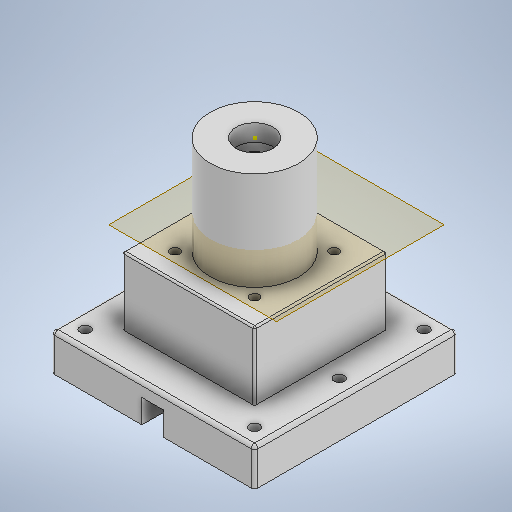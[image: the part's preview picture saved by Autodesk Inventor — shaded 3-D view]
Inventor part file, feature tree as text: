
AUTODESK INVENTOR PART (.ipt)
format: ipt  version: 2025.1 (Build 291241000, 241)  size: 374,272 bytes
history: native  units: mm
features: sketch x10, extrude x8, hole x2, fillet x2, plane x1
ambient origin geometry x8: Origin, YZ Plane, XZ Plane, XY Plane, X Axis, Y Axis, Z Axis, Center Point
bodies: Solid1 (feature_tree)
feature tree (23):
  sketch  "Sketch1"  dims[d0=120.0mm d1=120.0mm]
  extrude  "Extrusion1"  Depth=120.0mm
  extrude  "Extrusion2"  Depth=78.0mm
  hole  "Hole1"  [1 undecoded]
  extrude  "Extrusion3"  Depth=8.0mm TaperAngle=0.0deg
  fillet  "Fillet1"  Radius=2.0mm
  fillet  "Fillet2"  Radius=1.0mm
  hole  "Hole2"  [1 undecoded]
  extrude  "Extrusion4"  Depth=56.0mm
  sketch  "Sketch12"  dims[d57=47.0mm d58=47.0mm]
  extrude  "Extrusion9"  Depth=47.0mm
  sketch  "Sketch13"  dims[d59=20.0mm d60=38.3mm]
  extrude  "Extrusion10"  Depth=20.0mm
  extrude  "Extrusion8"  Depth=13.0mm
  extrude  "Extrusion11"  TaperAngle=0.0deg  [1 undecoded]
  plane  "Work Plane3"
  sketch  "Sketch15"  dims[d78=28.0mm d79=0.0mm d80=0.0mm d81=81.25mm d82=100.0mm d83=100.0mm d85=52.3mm d86=28.0mm d87=0.0mm d88=9.0mm d89=20.0mm d90=0.0mm d91=21.8mm d92=10.0mm d93=0.0mm d15=0.5mm d17=0.5mm d18=0.872665mm d35=0.0mm d36=0.0mm d37=0.0mm d38=0.0mm d73=0.5mm d74=0.872665mm d75=0.5mm d76=0.872665mm]
  sketch  "Sketch2"  dims[d13=78.0mm d14=78.0mm]
  sketch  "Sketch3"  dims[d16=0.0mm d20=0.0mm]
  sketch  "Sketch4"  dims[d21=6.1mm d22=6.0mm d23=4.0mm d24=2.0mm d25=90.0deg d26=15.0mm d27=0.0mm d28=8.0mm d29=8.0mm d30=0.0mm d31=0.0mm d33=2.0mm d34=1.0mm]
  sketch  "Sketch6"  dims[d46=5.5mm d47=6.0mm d48=4.0mm d49=2.0mm d50=90.0deg d51=8.0mm d52=0.0mm d53=56.0mm]
  sketch  "Sketch9"  dims[d54=56.0mm d56=38.3mm]
  sketch  "Sketch14"  dims[d61=5.0mm d62=5.0mm d63=0.0mm d64=0.0mm d77=13.0mm]
note: 3 required parameter values undecoded (feature->parameter linkage not recoverable at this tier; creation-order binding heuristic only, values carry confidence <= 0.55)
